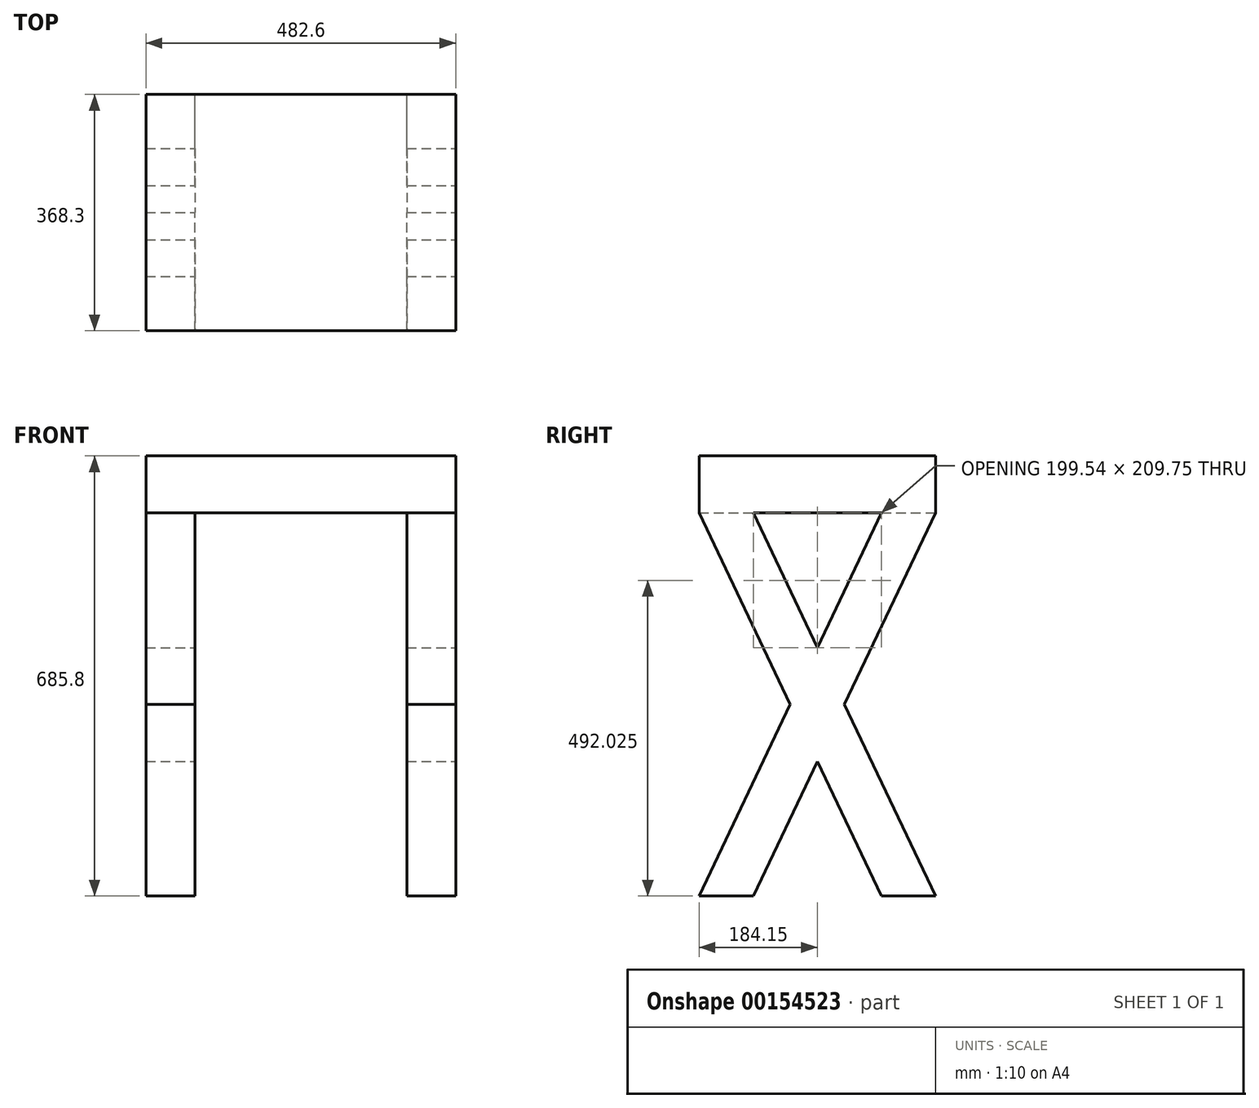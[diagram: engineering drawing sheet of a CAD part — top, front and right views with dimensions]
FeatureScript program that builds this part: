
annotation { "Feature Type Name" : "Feature", "Feature Type Description" : "" }
export const myFeature = defineFeature(function(context is Context, id is Id, definition is map)
    precondition{}
    {
        {
            var Q0;
            Q0=qCreatedBy(makeId("Top.planeOp"),FACE);
            var sketch = newSketch(context, id + "F0", { "sketchPlane" : qUnion([Q0])});
            skLineSegment(sketch, "E0.bottom", {"start": v(241.3, 184.15) * mm, "end": v(-241.3, 184.15) * mm});
            skLineSegment(sketch, "E0.top", {"start": v(241.3, -184.15) * mm, "end": v(-241.3, -184.15) * mm});
            skLineSegment(sketch, "E0.left", {"start": v(241.3, 184.15) * mm, "end": v(241.3, -184.15) * mm});
            skLineSegment(sketch, "E0.right", {"start": v(-241.3, 184.15) * mm, "end": v(-241.3, -184.15) * mm});
            skPoint(sketch, "E0.middle", {"position": v(0, 0) * mm});
            skSolve(sketch);
        }
        {
            var Q0;
            Q0 = qSketchRegion(id + "F0", true);
            extrude(context, id + "F1", {"entities" : qUnion([Q0]), "depth" : 88.9 * mm});
        }
        {
            var Q0;
            Q0=makeQuery(id+"F1.opExtrude","SWEPT_FACE",FACE,{"disambiguationData":[OSD([sQuery(id+"F0.wireOp",EDGE,"E0.left")])]});
            var sketch = newSketch(context, id + "F2", { "sketchPlane" : qUnion([Q0])});
            skLineSegment(sketch, "E1", {"start": v(-184.15, 0) * mm, "end": v(99.77, -596.9) * mm});
            skLineSegment(sketch, "E2", {"start": v(99.77, -596.9) * mm, "end": v(184.15, -596.9) * mm});
            skLineSegment(sketch, "E3", {"start": v(184.15, -596.9) * mm, "end": v(-99.77, 0) * mm});
            skLineSegment(sketch, "E4", {"start": v(-99.77, 0) * mm, "end": v(-184.15, 0) * mm});
            skLineSegment(sketch, "E5", {"start": v(184.15, 0) * mm, "end": v(-99.77, -596.9) * mm});
            skLineSegment(sketch, "E6", {"start": v(-99.77, -596.9) * mm, "end": v(-184.15, -596.9) * mm});
            skLineSegment(sketch, "E7", {"start": v(-184.15, -596.9) * mm, "end": v(99.77, 0) * mm});
            skLineSegment(sketch, "E8", {"start": v(99.77, 0) * mm, "end": v(184.15, 0) * mm});
            skSolve(sketch);
        }
        {
            var Q0;
            {var subQ0=sQuery(id+"F2.wireOp",EDGE,"E4");Q0=makeQuery(id+"F2.imprint","IMPRINT",FACE,{"disambiguationData":[TD([[makeQuery(id+"F2.imprint","IMPRINT",EDGE,{"derivedFrom":subQ0}),1.0]])]});}
            var Q1;
            {var subQ5=sQuery(id+"F2.wireOp",EDGE,"E8");Q1=makeQuery(id+"F2.imprint","IMPRINT",FACE,{"disambiguationData":[TD([[makeQuery(id+"F2.imprint","IMPRINT",EDGE,{"derivedFrom":subQ5}),1.0]])]});}
            var Q2;
            {var subQ0=sQuery(id+"F2.wireOp",EDGE,"E7");var subQ1=sQuery(id+"F2.wireOp",EDGE,"E1");var subQ2=makeQuery(id+"F2.imprint","INTERSECT",VERTEX,{"derivedFrom":[subQ1,subQ0]});Q2=makeQuery(id+"F2.imprint","IMPRINT",FACE,{"disambiguationData":[TD([[makeQuery(id+"F2.imprint","IMPRINT",EDGE,{"disambiguationData":[TD([[subQ2,-1.0]])],"derivedFrom":subQ1}),1.0]])]});}
            var Q3;
            {var subQ0=sQuery(id+"F2.wireOp",EDGE,"E2");Q3=makeQuery(id+"F2.imprint","IMPRINT",FACE,{"disambiguationData":[TD([[makeQuery(id+"F2.imprint","IMPRINT",EDGE,{"derivedFrom":subQ0}),1.0]])]});}
            var Q4;
            {var subQ5=sQuery(id+"F2.wireOp",EDGE,"E6");Q4=makeQuery(id+"F2.imprint","IMPRINT",FACE,{"disambiguationData":[TD([[makeQuery(id+"F2.imprint","IMPRINT",EDGE,{"derivedFrom":subQ5}),-1.0]])]});}
            extrude(context, id + "F3", {"entities" : qUnion([Q0, Q1, Q2, Q3, Q4]), "operationType" : NewBodyOperationType.ADD, "oppositeDirection" : true, "depth" : 482.6 * mm});
        }
        {
            var Q0;
            Q0=makeQuery(id+"F1.opExtrude","SWEPT_FACE",FACE,{"disambiguationData":[OSD([sQuery(id+"F0.wireOp",EDGE,"E0.bottom")])]});
            var sketch = newSketch(context, id + "F4", { "sketchPlane" : qUnion([Q0])});
            skLineSegment(sketch, "E9.bottom", {"start": v(-165.1, 0) * mm, "end": v(165.1, 0) * mm});
            skLineSegment(sketch, "E9.top", {"start": v(-165.1, -596.9) * mm, "end": v(165.1, -596.9) * mm});
            skLineSegment(sketch, "E9.left", {"start": v(-165.1, 0) * mm, "end": v(-165.1, -596.9) * mm});
            skLineSegment(sketch, "E9.right", {"start": v(165.1, 0) * mm, "end": v(165.1, -596.9) * mm});
            skSolve(sketch);
        }
        {
            var Q0;
            Q0=makeQuery(id+"F4.imprint","IMPRINT",FACE,{"disambiguationData":[TD([[makeQuery(id+"F4.imprint","IMPRINT",EDGE,{"derivedFrom":sQuery(id+"F4.wireOp",EDGE,"E9.bottom")}),-1.0]])]});
            extrude(context, id + "F5", {"entities" : qUnion([Q0]), "operationType" : NewBodyOperationType.REMOVE, "endBound" : BoundingType.THROUGH_ALL, "oppositeDirection" : true, "depth" : 30.48 * mm});
        }
    });
